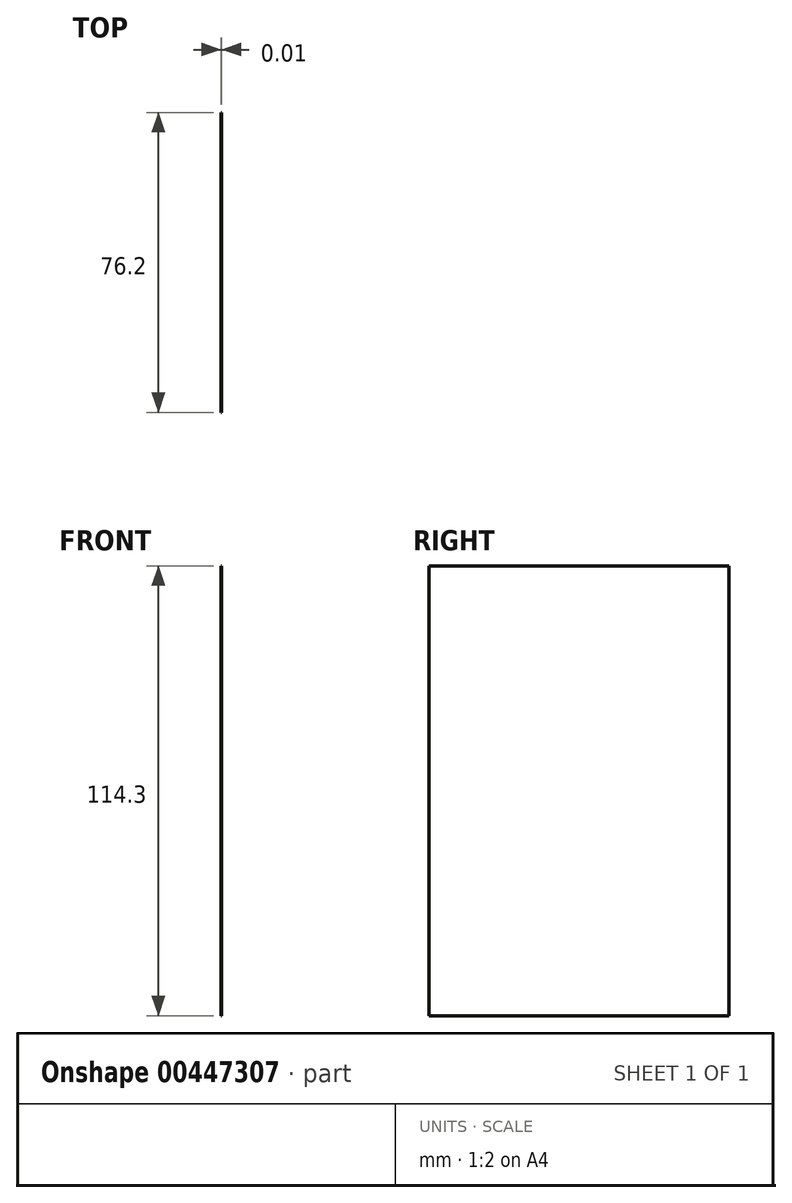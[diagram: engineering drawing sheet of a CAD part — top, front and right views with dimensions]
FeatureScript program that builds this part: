
annotation { "Feature Type Name" : "Feature", "Feature Type Description" : "" }
export const myFeature = defineFeature(function(context is Context, id is Id, definition is map)
    precondition{}
    {
        {
            var Q0;
            Q0=qCreatedBy(makeId("Right.planeOp"),FACE);
            var sketch = newSketch(context, id + "F0", { "sketchPlane" : qUnion([Q0])});
            skLineSegment(sketch, "E0.bottom", {"start": v(-38.1, 57.15) * mm, "end": v(38.1, 57.15) * mm});
            skLineSegment(sketch, "E0.top", {"start": v(-38.1, -57.15) * mm, "end": v(38.1, -57.15) * mm});
            skLineSegment(sketch, "E0.left", {"start": v(-38.1, 57.15) * mm, "end": v(-38.1, -57.15) * mm});
            skLineSegment(sketch, "E0.right", {"start": v(38.1, 57.15) * mm, "end": v(38.1, -57.15) * mm});
            skPoint(sketch, "E0.middle", {"position": v(0, 0) * mm});
            skSolve(sketch);
        }
        {
            var Q0;
            Q0 = qSketchRegion(id + "F0", true);
            extrude(context, id + "F1", {"entities" : qUnion([Q0]), "depth" : 3 / 203.2 * mm});
        }
    });
